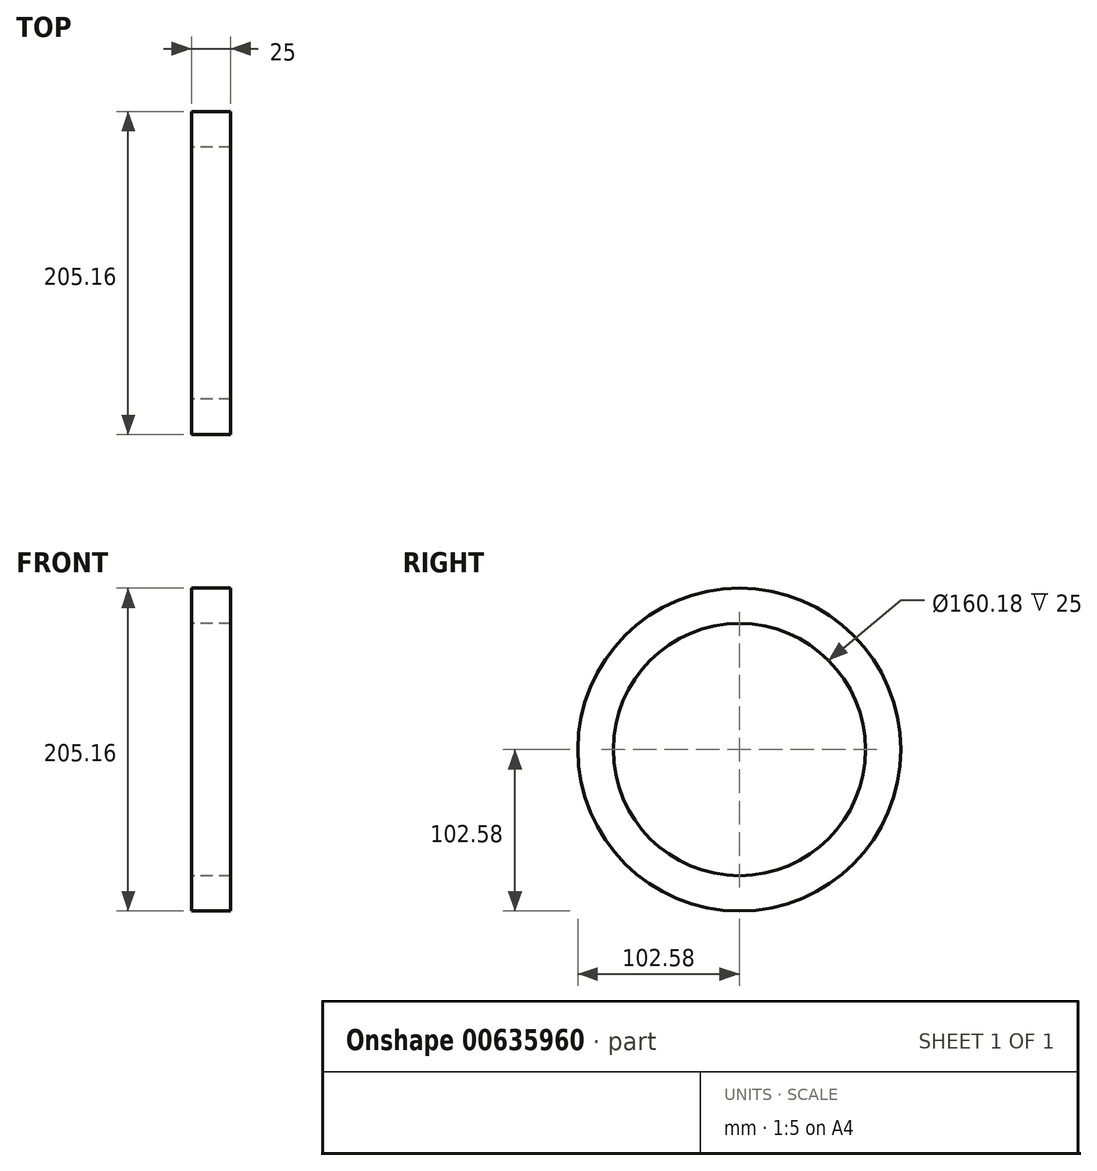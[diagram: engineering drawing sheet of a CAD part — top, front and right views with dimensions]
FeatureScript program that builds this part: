
annotation { "Feature Type Name" : "Feature", "Feature Type Description" : "" }
export const myFeature = defineFeature(function(context is Context, id is Id, definition is map)
    precondition{}
    {
        {
            var Q0;
            Q0=qCreatedBy(makeId("Right.planeOp"),FACE);
            var sketch = newSketch(context, id + "F0", { "sketchPlane" : qUnion([Q0])});
            skCircle(sketch, "E0", {"center": v(0, 0) * mm, "radius": 102.58 * mm});
            skCircle(sketch, "E1", {"center": v(0, 0) * mm, "radius": 80.09 * mm});
            skSolve(sketch);
        }
        {
            var Q0;
            Q0=makeQuery(id+"F0.imprint","IMPRINT",FACE,{"disambiguationData":[TD([[makeQuery(id+"F0.imprint","IMPRINT",EDGE,{"derivedFrom":sQuery(id+"F0.wireOp",EDGE,"E0")}),1.0]])]});
            extrude(context, id + "F1", {"entities" : qUnion([Q0]), "depth" : 25 * mm, "offsetDistance" : 25 * mm});
        }
    });
